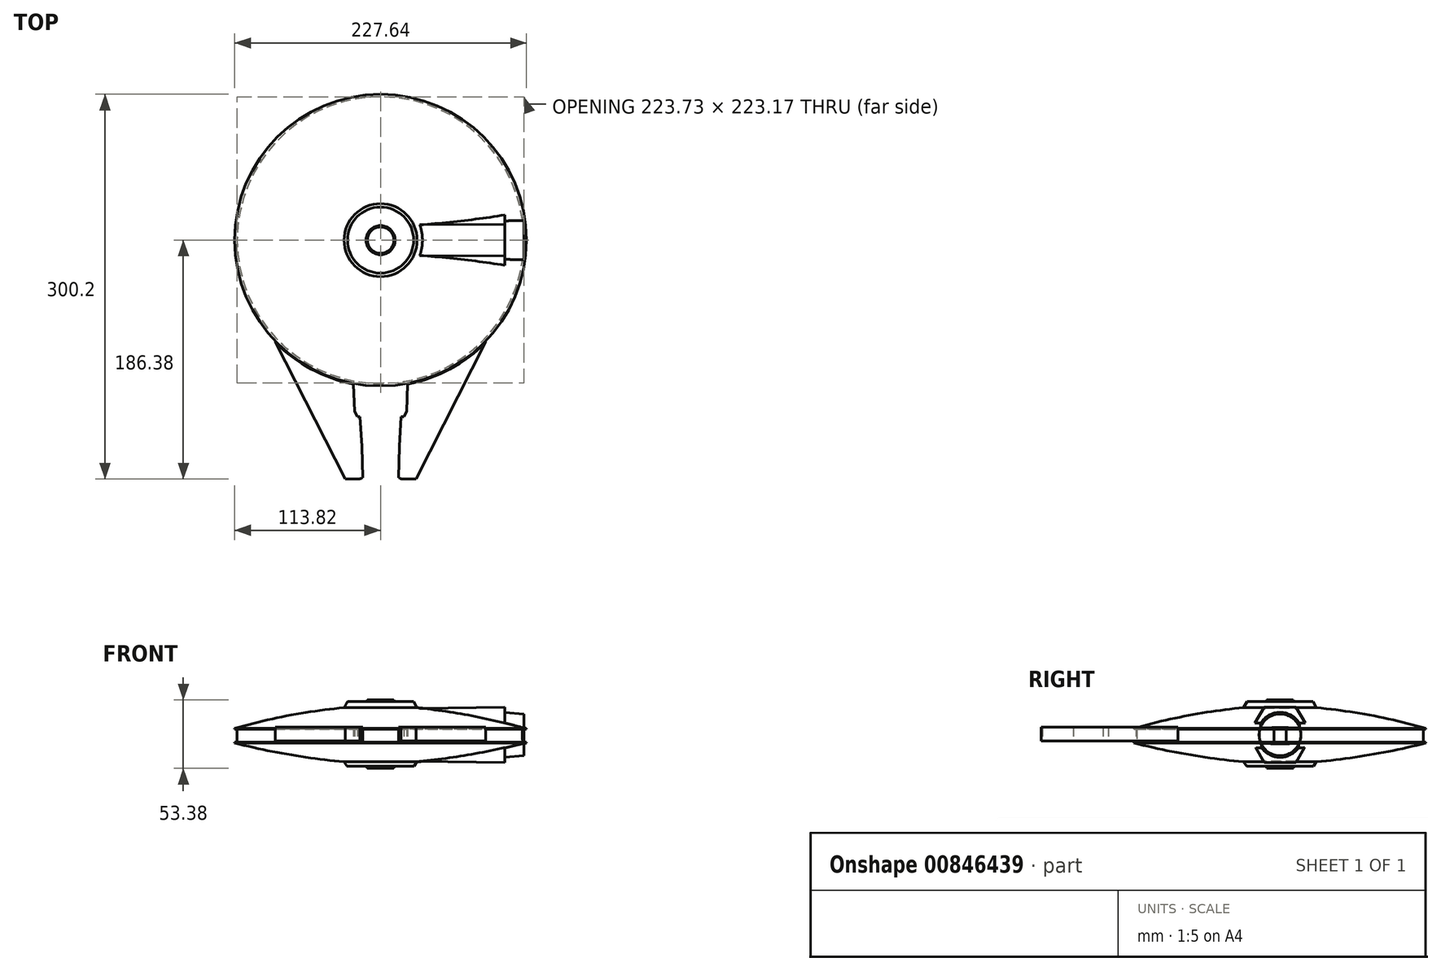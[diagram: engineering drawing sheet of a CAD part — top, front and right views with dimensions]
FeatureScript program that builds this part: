
annotation { "Feature Type Name" : "Feature", "Feature Type Description" : "" }
export const myFeature = defineFeature(function(context is Context, id is Id, definition is map)
    precondition{}
    {
        {
            var Q0;
            Q0=qCreatedBy(makeId("Top.planeOp"),FACE);
            var sketch = newSketch(context, id + "F0", { "sketchPlane" : qUnion([Q0])});
            skCircle(sketch, "E0", {"center": v(0, 0) * mm, "radius": 114.3 * mm});
            skCircle(sketch, "E1", {"center": v(0, 0) * mm, "radius": 111.86 * mm});
            skLineSegment(sketch, "E2", {"start": v(-26.34, -190.26) * mm, "end": v(-16.28, -190.26) * mm});
            skLineSegment(sketch, "E3", {"start": v(-16.28, -190.26) * mm, "end": v(-16.28, -186.38) * mm});
            skLineSegment(sketch, "E4", {"start": v(-16.28, -186.38) * mm, "end": v(-26.34, -186.38) * mm});
            skLineSegment(sketch, "E5", {"start": v(-26.34, -186.38) * mm, "end": v(-26.34, -190.26) * mm});
            skLineSegment(sketch, "E6", {"start": v(-26.34, -188.32) * mm, "end": v(-28.08, -189.59) * mm});
            skLineSegment(sketch, "E7", {"start": v(-28.08, -189.59) * mm, "end": v(-31.15, -185.38) * mm});
            skLineSegment(sketch, "E8", {"start": v(-31.15, -185.38) * mm, "end": v(-43.66, -160.8) * mm});
            skLineSegment(sketch, "E9", {"start": v(-43.66, -160.8) * mm, "end": v(-89.03, -71.68) * mm});
            skLineSegment(sketch, "E10", {"start": v(-89.03, -71.68) * mm, "end": v(-31.15, -185.38) * mm});
            skLineSegment(sketch, "E11", {"start": v(-21.3, -107.15) * mm, "end": v(-20.3, -133.82) * mm});
            skPoint(sketch, "E11.startSnap0", {"position": v(-21.3, -190.26) * mm});
            skLineSegment(sketch, "E12", {"start": v(-20.3, -133.82) * mm, "end": v(-18.03, -137.97) * mm});
            skLineSegment(sketch, "E13", {"start": v(-18.03, -137.97) * mm, "end": v(-15.97, -137.97) * mm});
            skLineSegment(sketch, "E14", {"start": v(-15.97, -137.97) * mm, "end": v(-14.7, -161.14) * mm});
            skLineSegment(sketch, "E15", {"start": v(-14.7, -161.14) * mm, "end": v(-13.92, -185.42) * mm});
            skLineSegment(sketch, "E16", {"start": v(-13.92, -185.42) * mm, "end": v(-14.95, -185.42) * mm});
            skLineSegment(sketch, "E17", {"start": v(-14.95, -185.42) * mm, "end": v(-14.95, -186.02) * mm});
            skLineSegment(sketch, "E18", {"start": v(-14.95, -186.02) * mm, "end": v(-15.97, -186.02) * mm});
            skLineSegment(sketch, "E19", {"start": v(-15.97, -186.02) * mm, "end": v(-15.97, -186.38) * mm});
            skLineSegment(sketch, "E20", {"start": v(-15.97, -186.38) * mm, "end": v(-16.28, -186.38) * mm});
            skLineSegment(sketch, "E21", {"start": v(-89.03, -71.68) * mm, "end": v(-96.9, -55.9) * mm});
            skLineSegment(sketch, "E22", {"start": v(-96.9, -55.9) * mm, "end": v(-21.3, -107.15) * mm});
            skLineSegment(sketch, "E23", {"start": v(-26.34, -186.38) * mm, "end": v(-27.7, -186.38) * mm});
            skLineSegment(sketch, "E24", {"start": v(-27.7, -186.38) * mm, "end": v(-51.07, -140.46) * mm});
            skLineSegment(sketch, "E25", {"start": v(-51.07, -140.46) * mm, "end": v(-82.08, -79.55) * mm});
            skLineSegment(sketch, "E26", {"start": v(-82.08, -79.55) * mm, "end": v(-92.65, -58.78) * mm});
            skLineSegment(sketch, "E27", {"start": v(0, 0) * mm, "end": v(0, -150.43) * mm, "construction": true});
            skLineSegment(sketch, "E28.MirrorCS", {"start": v(28.08, -189.59) * mm, "end": v(31.15, -185.38) * mm});
            skLineSegment(sketch, "E29.MirrorCS", {"start": v(27.7, -186.38) * mm, "end": v(51.07, -140.46) * mm});
            skLineSegment(sketch, "E30.MirrorCS", {"start": v(26.34, -186.38) * mm, "end": v(27.7, -186.38) * mm});
            skLineSegment(sketch, "E31.MirrorCS", {"start": v(26.34, -188.32) * mm, "end": v(28.08, -189.59) * mm});
            skLineSegment(sketch, "E32.MirrorCS", {"start": v(26.34, -186.38) * mm, "end": v(26.34, -190.26) * mm});
            skLineSegment(sketch, "E33.MirrorCS", {"start": v(26.34, -190.26) * mm, "end": v(16.28, -190.26) * mm});
            skLineSegment(sketch, "E34.MirrorCS", {"start": v(16.28, -190.26) * mm, "end": v(16.28, -186.38) * mm});
            skLineSegment(sketch, "E35.MirrorCS", {"start": v(16.28, -186.38) * mm, "end": v(26.34, -186.38) * mm});
            skLineSegment(sketch, "E36.MirrorCS", {"start": v(15.97, -186.38) * mm, "end": v(16.28, -186.38) * mm});
            skLineSegment(sketch, "E37.MirrorCS", {"start": v(15.97, -186.02) * mm, "end": v(15.97, -186.38) * mm});
            skLineSegment(sketch, "E38.MirrorCS", {"start": v(14.95, -186.02) * mm, "end": v(15.97, -186.02) * mm});
            skLineSegment(sketch, "E39.MirrorCS", {"start": v(14.95, -185.42) * mm, "end": v(14.95, -186.02) * mm});
            skLineSegment(sketch, "E40.MirrorCS", {"start": v(13.92, -185.42) * mm, "end": v(14.95, -185.42) * mm});
            skLineSegment(sketch, "E41.MirrorCS", {"start": v(14.7, -161.14) * mm, "end": v(13.92, -185.42) * mm});
            skLineSegment(sketch, "E42.MirrorCS", {"start": v(15.97, -137.97) * mm, "end": v(14.7, -161.14) * mm});
            skLineSegment(sketch, "E43.MirrorCS", {"start": v(18.03, -137.97) * mm, "end": v(15.97, -137.97) * mm});
            skLineSegment(sketch, "E44.MirrorCS", {"start": v(20.3, -133.82) * mm, "end": v(18.03, -137.97) * mm});
            skLineSegment(sketch, "E45.MirrorCS", {"start": v(21.3, -107.15) * mm, "end": v(20.3, -133.82) * mm});
            skLineSegment(sketch, "E46.MirrorCS", {"start": v(51.07, -140.46) * mm, "end": v(82.08, -79.55) * mm});
            skLineSegment(sketch, "E47.MirrorCS", {"start": v(89.03, -71.68) * mm, "end": v(31.15, -185.38) * mm});
            skLineSegment(sketch, "E48.MirrorCS", {"start": v(82.08, -79.55) * mm, "end": v(92.65, -58.78) * mm});
            skLineSegment(sketch, "E49.MirrorCS", {"start": v(96.9, -55.9) * mm, "end": v(21.3, -107.15) * mm});
            skLineSegment(sketch, "E50.MirrorCS", {"start": v(89.03, -71.68) * mm, "end": v(96.9, -55.9) * mm});
            skCircle(sketch, "E51", {"center": v(0, 0) * mm, "radius": 28.4 * mm});
            skLineSegment(sketch, "E52.bottom", {"start": v(31, 10.07) * mm, "end": v(96.69, 10.07) * mm});
            skLineSegment(sketch, "E52.top", {"start": v(31, -9.98) * mm, "end": v(96.69, -9.98) * mm});
            skLineSegment(sketch, "E52.left", {"start": v(31, 10.07) * mm, "end": v(31, -9.98) * mm});
            skLineSegment(sketch, "E52.right", {"start": v(96.69, 10.07) * mm, "end": v(96.69, -9.98) * mm});
            skLineSegment(sketch, "E53", {"start": v(96.69, 10.07) * mm, "end": v(96.69, 17.49) * mm, "construction": true});
            skLineSegment(sketch, "E54", {"start": v(96.69, 17.49) * mm, "end": v(29.41, 11.54) * mm, "construction": true});
            skLineSegment(sketch, "E55", {"start": v(29.41, 11.54) * mm, "end": v(29.41, -11.47) * mm, "construction": true});
            skLineSegment(sketch, "E56", {"start": v(29.41, -11.47) * mm, "end": v(96.69, -17.87) * mm, "construction": true});
            skLineSegment(sketch, "E57", {"start": v(96.69, -17.87) * mm, "end": v(96.69, -9.98) * mm, "construction": true});
            skSolve(sketch);
        }
        {
            var Q0;
            Q0=qCreatedBy(makeId("Front.planeOp"),FACE);
            var sketch = newSketch(context, id + "F1", { "sketchPlane" : qUnion([Q0])});
            skLineSegment(sketch, "E58", {"start": v(0, 0) * mm, "end": v(114.3, 0) * mm, "construction": true});
            skLineSegment(sketch, "E59", {"start": v(0, 0) * mm, "end": v(0, 60.72) * mm, "construction": true});
            skLineSegment(sketch, "E60", {"start": v(111.86, -6.89) * mm, "end": v(111.86, 3.2) * mm});
            skLineSegment(sketch, "E61", {"start": v(111.86, 3.2) * mm, "end": v(0, 3.2) * mm});
            skLineSegment(sketch, "E62", {"start": v(111.86, -6.89) * mm, "end": v(0, -6.89) * mm});
            skLineSegment(sketch, "E63", {"start": v(0, -6.89) * mm, "end": v(0, 3.2) * mm});
            skLineSegment(sketch, "E64", {"start": v(113.82, 3.84) * mm, "end": v(113.82, 3.2) * mm});
            skLineSegment(sketch, "E65", {"start": v(113.82, 3.84) * mm, "end": v(0, 3.84) * mm});
            skLineSegment(sketch, "E66", {"start": v(0, 3.84) * mm, "end": v(0, 3.2) * mm});
            skLineSegment(sketch, "E67", {"start": v(113.82, 3.2) * mm, "end": v(0, 3.2) * mm});
            skLineSegment(sketch, "E68", {"start": v(111.86, -6.89) * mm, "end": v(113.82, -6.89) * mm});
            skLineSegment(sketch, "E69", {"start": v(113.82, -6.89) * mm, "end": v(113.82, -7.55) * mm});
            skLineSegment(sketch, "E70", {"start": v(113.82, -7.55) * mm, "end": v(0, -7.55) * mm});
            skLineSegment(sketch, "E71", {"start": v(0, -7.55) * mm, "end": v(0, -6.89) * mm});
            skPoint(sketch, "E72", {"position": v(-26.13, 24.73) * mm});
            skLineSegment(sketch, "E73", {"start": v(25.77, 24.78) * mm, "end": v(0, 24.78) * mm});
            skLineSegment(sketch, "E74", {"start": v(25.77, 24.78) * mm, "end": v(28.46, 20.04) * mm});
            skArc(sketch, "E75", {"start": v(113.82, 3.84) * mm, "mid": v(71.53, 13.97) * mm, "end": v(28.46, 20.04) * mm});
            skLineSegment(sketch, "E76", {"start": v(0, 24.78) * mm, "end": v(0, -25.77) * mm});
            skLineSegment(sketch, "E77", {"start": v(0, -25.77) * mm, "end": v(26.05, -25.77) * mm});
            skLineSegment(sketch, "E78", {"start": v(26.05, -25.77) * mm, "end": v(28.46, -22.3) * mm});
            skArc(sketch, "E79", {"start": v(28.46, -22.3) * mm, "mid": v(71.42, -16.56) * mm, "end": v(113.82, -7.55) * mm});
            skLineSegment(sketch, "E80", {"start": v(0, -25.77) * mm, "end": v(0, -27.34) * mm});
            skLineSegment(sketch, "E81", {"start": v(11.31, -25.77) * mm, "end": v(11.31, -26.34) * mm});
            skLineSegment(sketch, "E82", {"start": v(11.31, -26.34) * mm, "end": v(10.58, -26.34) * mm});
            skLineSegment(sketch, "E83", {"start": v(10.58, -26.34) * mm, "end": v(10.58, -26.97) * mm});
            skLineSegment(sketch, "E84", {"start": v(10.58, -26.97) * mm, "end": v(10.36, -26.97) * mm});
            skLineSegment(sketch, "E85", {"start": v(10.36, -26.97) * mm, "end": v(10.36, -27.34) * mm});
            skLineSegment(sketch, "E86", {"start": v(10.36, -27.34) * mm, "end": v(0, -27.34) * mm});
            skPoint(sketch, "E87.orphan", {"position": v(0, -27.57) * mm});
            skLineSegment(sketch, "E88", {"start": v(11.37, 24.78) * mm, "end": v(11.37, 25.03) * mm});
            skLineSegment(sketch, "E89", {"start": v(11.37, 25.03) * mm, "end": v(10.61, 25.03) * mm});
            skLineSegment(sketch, "E90", {"start": v(10.61, 25.03) * mm, "end": v(10.61, 25.58) * mm});
            skLineSegment(sketch, "E91", {"start": v(10.61, 25.58) * mm, "end": v(10.3, 25.58) * mm});
            skLineSegment(sketch, "E92", {"start": v(10.3, 25.58) * mm, "end": v(10.3, 26.04) * mm});
            skLineSegment(sketch, "E93", {"start": v(10.3, 26.04) * mm, "end": v(0, 26.04) * mm});
            skLineSegment(sketch, "E94", {"start": v(0, 26.04) * mm, "end": v(0, 24.78) * mm});
            skPoint(sketch, "E95", {"position": v(0, -1.2) * mm});
            skSolve(sketch);
        }
        {
            var Q0;
            Q0=qCreatedBy(makeId("Right.planeOp"),FACE);
            var sketch = newSketch(context, id + "F2", { "sketchPlane" : qUnion([Q0])});
            skPoint(sketch, "E96", {"position": v(0, -1.16) * mm});
            skCircle(sketch, "E97", {"center": v(0, -1.16) * mm, "radius": 26.03 * mm});
            skSolve(sketch);
        }
        {
            var Q0;
            Q0=makeQuery(id+"F1.imprint","IMPRINT",FACE,{"disambiguationData":[TD([[makeQuery(id+"F1.imprint","IMPRINT",EDGE,{"derivedFrom":sQuery(id+"F1.wireOp",EDGE,"E60")}),1.0]])]});
            var Q1;
            Q1=sQuery(id+"F1.wireOp",EDGE,"E63");
            revolve(context, id + "F3", {"surfaceOperationType" : NewSurfaceOperationType.NEW, "entities" : qUnion([Q0]), "axis" : qUnion([Q1]), "revolveType" : RevolveType.FULL});
        }
        {
            var Q0;
            Q0=makeQuery(id+"F1.imprint","IMPRINT",FACE,{"disambiguationData":[TD([[makeQuery(id+"F1.imprint","IMPRINT",EDGE,{"derivedFrom":sQuery(id+"F1.wireOp",EDGE,"E61")}),-1.0]])]});
            var Q1;
            Q1=sQuery(id+"F1.wireOp",EDGE,"E66");
            revolve(context, id + "F4", {"operationType" : NewBodyOperationType.ADD, "surfaceOperationType" : NewSurfaceOperationType.NEW, "entities" : qUnion([Q0]), "axis" : qUnion([Q1]), "revolveType" : RevolveType.FULL});
        }
        {
            var Q0;
            Q0=makeQuery(id+"F1.imprint","IMPRINT",FACE,{"disambiguationData":[TD([[makeQuery(id+"F1.imprint","IMPRINT",EDGE,{"derivedFrom":sQuery(id+"F1.wireOp",EDGE,"E62")}),1.0]])]});
            var Q1;
            Q1=sQuery(id+"F1.wireOp",EDGE,"E71");
            revolve(context, id + "F5", {"operationType" : NewBodyOperationType.ADD, "surfaceOperationType" : NewSurfaceOperationType.NEW, "entities" : qUnion([Q0]), "axis" : qUnion([Q1]), "revolveType" : RevolveType.FULL});
        }
        {
            var Q0;
            {var subQ0=makeQuery(id+"F1.imprint","IMPRINT",EDGE,{"derivedFrom":sQuery(id+"F1.wireOp",EDGE,"E61")});var subQ1=makeQuery(id+"F1.imprint","IMPRINT",EDGE,{"derivedFrom":sQuery(id+"F1.wireOp",EDGE,"E62")});var subQ7=sQuery(id+"F1.wireOp",EDGE,"E88");var subQ10=sQuery(id+"F1.wireOp",EDGE,"E65");var subQ11=makeQuery(id+"F1.imprint","IMPRINT",EDGE,{"derivedFrom":subQ10});var subQ14=sQuery(id+"F1.wireOp",EDGE,"E80");var subQ19=sQuery(id+"F1.wireOp",EDGE,"E70");var subQ20=makeQuery(id+"F1.imprint","IMPRINT",EDGE,{"derivedFrom":subQ19});Q0=qUnion([makeQuery(id+"F1.imprint","IMPRINT",FACE,{"disambiguationData":[TD([[subQ0,-1.0]])]}),makeQuery(id+"F1.imprint","IMPRINT",FACE,{"disambiguationData":[TD([[subQ20,1.0]])]}),makeQuery(id+"F1.imprint","IMPRINT",FACE,{"disambiguationData":[TD([[makeQuery(id+"F1.imprint","IMPRINT",EDGE,{"derivedFrom":subQ7}),1.0]])]}),makeQuery(id+"F1.imprint","IMPRINT",FACE,{"disambiguationData":[TD([[subQ1,1.0]])]}),makeQuery(id+"F1.imprint","IMPRINT",FACE,{"disambiguationData":[TD([[makeQuery(id+"F1.imprint","IMPRINT",EDGE,{"derivedFrom":subQ14}),1.0]])]}),makeQuery(id+"F1.imprint","IMPRINT",FACE,{"disambiguationData":[TD([[subQ11,-1.0]])]}),makeQuery(id+"F1.imprint","IMPRINT",FACE,{"disambiguationData":[TD([[makeQuery(id+"F1.imprint","IMPRINT",EDGE,{"derivedFrom":sQuery(id+"F1.wireOp",EDGE,"E60")}),1.0]])]})]);}
            var Q1;
            Q1=sQuery(id+"F1.wireOp",EDGE,"E59");
            revolve(context, id + "F6", {"operationType" : NewBodyOperationType.ADD, "surfaceOperationType" : NewSurfaceOperationType.NEW, "entities" : qUnion([Q0]), "axis" : qUnion([Q1]), "revolveType" : RevolveType.FULL});
        }
        {
            var Q0;
            Q0=makeQuery(id+"F0.imprint","IMPRINT",FACE,{"disambiguationData":[TD([[makeQuery(id+"F0.imprint","IMPRINT",EDGE,{"derivedFrom":sQuery(id+"F0.wireOp",EDGE,"E4")}),-1.0]])]});
            var Q1;
            {var subQ0=sQuery(id+"F0.wireOp",EDGE,"E46.MirrorCS");Q1=makeQuery(id+"F0.imprint","IMPRINT",FACE,{"disambiguationData":[TD([[makeQuery(id+"F0.imprint","IMPRINT",EDGE,{"derivedFrom":subQ0}),1.0]])]});}
            extrude(context, id + "F7", {"entities" : qUnion([Q0, Q1]), "depth" : 4.9 * mm, "offsetDistance" : 25.4 * mm, "hasSecondDirection" : true, "secondDirectionOppositeDirection" : true, "secondDirectionDepth" : 5.84 * mm});
        }
        {
            var Q0;
            Q0 = qSketchRegion(id + "F2", true);
            extrude(context, id + "F8", {"entities" : qUnion([Q0]), "operationType" : NewBodyOperationType.ADD, "depth" : 111.76 * mm, "offsetDistance" : 25.4 * mm, "hasDraft" : true, "draftAngle" : 5 * degree, "draftPullDirection" : true, "hasSecondDirection" : true, "secondDirectionOppositeDirection" : false, "secondDirectionDepth" : 86.61 * mm});
        }
        {
            var Q0;
            Q0=qCreatedBy(makeId("Right.planeOp"),FACE);
            cPlane(context, id + "F9", {"entities" : qUnion([Q0]), "cplaneType" : CPlaneType.OFFSET, "offset" : 96.77 * mm, "width" : 152.4 * mm, "height" : 152.4 * mm});
        }
        {
            var Q0;
            Q0=qCreatedBy(id+"F9.planeOp",FACE);
            var sketch = newSketch(context, id + "F10", { "sketchPlane" : qUnion([Q0])});
            skCircle(sketch, "E98.cCircle", {"center": v(0, -1.14) * mm, "radius": 21.56 * mm, "construction": true});
            skLineSegment(sketch, "E98.0", {"start": v(-12.45, 20.42) * mm, "end": v(12.45, 20.42) * mm});
            skLineSegment(sketch, "E98.1", {"start": v(12.45, 20.42) * mm, "end": v(24.9, -1.14) * mm});
            skLineSegment(sketch, "E98.2", {"start": v(24.9, -1.14) * mm, "end": v(12.45, -22.7) * mm});
            skLineSegment(sketch, "E98.3", {"start": v(12.45, -22.7) * mm, "end": v(-12.45, -22.7) * mm});
            skLineSegment(sketch, "E98.4", {"start": v(-12.45, -22.7) * mm, "end": v(-24.9, -1.14) * mm});
            skLineSegment(sketch, "E98.5", {"start": v(-24.9, -1.14) * mm, "end": v(-12.45, 20.42) * mm});
            skPoint(sketch, "E98.0.midPoint", {"position": v(0, 20.42) * mm});
            skSolve(sketch);
        }
        {
            var Q0;
            Q0 = qSketchRegion(id + "F10", true);
            extrude(context, id + "F11", {"entities" : qUnion([Q0]), "operationType" : NewBodyOperationType.ADD, "oppositeDirection" : true, "depth" : 78.23 * mm, "offsetDistance" : 25.4 * mm, "hasDraft" : true, "draftAngle" : 0.7 * degree, "draftPullDirection" : true});
        }
    });
